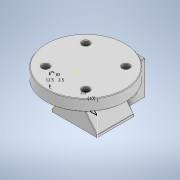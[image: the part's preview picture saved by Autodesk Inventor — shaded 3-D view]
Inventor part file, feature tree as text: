
AUTODESK INVENTOR PART (.ipt)
format: ipt  version: 2021 (Build 250183000, 183)  size: 331,776 bytes
history: native  units: mm
features: sketch x8, extrude x6, fillet x2
ambient origin geometry x8: Origin, YZ Plane, XZ Plane, XY Plane, X Axis, Y Axis, Z Axis, Center Point
bodies: Solid1 (feature_tree)
feature tree (16):
  sketch  "Sketch1"  dims[d0=70.0mm d1=10.0mm d2=0.0mm]
  extrude  "Extrusion1"  Depth=10.0mm TaperAngle=0.0deg
  extrude  "Extrusion4"  Depth=6.0mm
  extrude  "Extrusion2"  Depth=25.0mm TaperAngle=0.0deg
  extrude  "Extrusion9"  Depth=10.0mm
  sketch  "Sketch8"  dims[d20=40.0mm d21=52.5mm d22=40.0mm]
  extrude  "Extrusion8"  Depth=52.5mm
  fillet  "Fillet1"  Radius=40.0mm
  extrude  "Extrusion10"  Depth=10.0mm
  fillet  "Fillet2"  Radius=2.5mm
  sketch  "Sketch2"  dims[d3=25.0mm d4=6.0mm]
  sketch  "Sketch3"  dims[d5=40.0mm d7=360.0deg d9=25.0mm d10=0.0mm]
  sketch  "Sketch5"  dims[d18=20.0mm d19=10.0mm]
  sketch  "Sketch12"  dims[d23=30.0mm d24=0.0mm d33=10.0mm d34=2.5mm]
  sketch  "Sketch13"  dims[d35=12.5mm]
  sketch  "Sketch14"  dims[d39=10.0mm d40=2.5mm d48=10.0mm d49=10.0mm d50=20.0mm d51=0.0mm d52=0.5mm d53=2.5mm d54=12.5mm d55=10.0mm d56=20.0mm d57=2.5mm d58=0.0mm d59=0.0mm d60=6.25mm d61=10.0mm d62=6.0mm d63=0.0mm d64=0.0mm d65=0.5mm d41=0.5mm d42=0.872665mm d43=0.5mm d44=0.872665mm]
